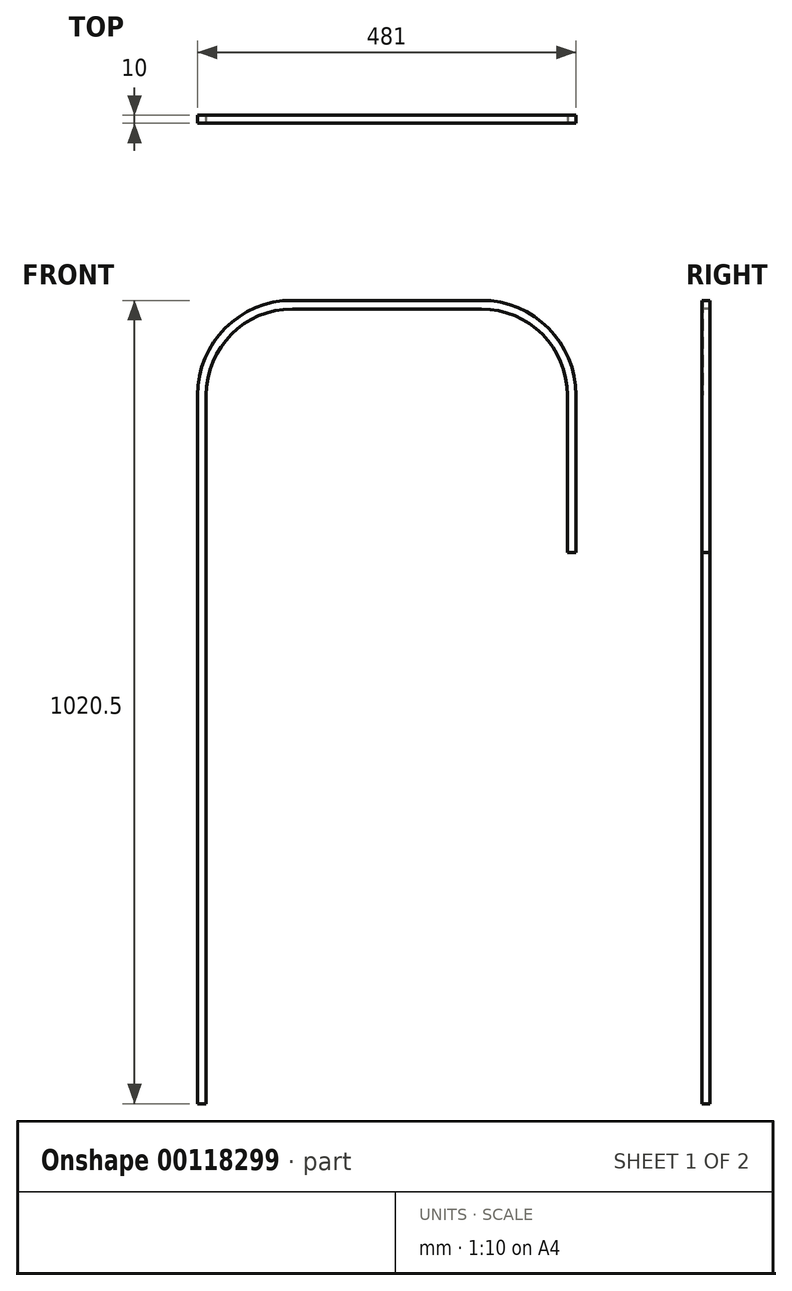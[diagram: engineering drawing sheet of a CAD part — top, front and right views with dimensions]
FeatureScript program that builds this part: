
annotation { "Feature Type Name" : "Feature", "Feature Type Description" : "" }
export const myFeature = defineFeature(function(context is Context, id is Id, definition is map)
    precondition{}
    {
        {
            var Q0;
            Q0=qCreatedBy(makeId("Front.planeOp"),FACE);
            var sketch = newSketch(context, id + "F0", { "sketchPlane" : qUnion([Q0])});
            skPoint(sketch, "E0.middle", {"position": v(15.73, 0) * mm});
            skLineSegment(sketch, "E1", {"start": v(-304.27, 450) * mm, "end": v(-302.77, 450) * mm});
            skLineSegment(sketch, "E2", {"start": v(197.23, 450) * mm, "end": v(198.73, 450) * mm});
            skLineSegment(sketch, "E3.0.left", {"start": v(-172.77, 570.5) * mm, "end": v(67.23, 570.5) * mm});
            skLineSegment(sketch, "E3.0.right", {"start": v(-172.77, 559.5) * mm, "end": v(67.23, 559.5) * mm});
            skArc(sketch, "E3.1.left", {"start": v(-172.77, 559.5) * mm, "mid": v(-250.2, 527.43) * mm, "end": v(-282.27, 450) * mm});
            skArc(sketch, "E3.1.right", {"start": v(-172.77, 570.5) * mm, "mid": v(-257.97, 535.2) * mm, "end": v(-293.27, 450) * mm});
            skArc(sketch, "E3.2.left", {"start": v(176.73, 450) * mm, "mid": v(144.66, 527.43) * mm, "end": v(67.23, 559.5) * mm});
            skArc(sketch, "E3.2.right", {"start": v(187.73, 450) * mm, "mid": v(152.44, 535.2) * mm, "end": v(67.23, 570.5) * mm});
            skLineSegment(sketch, "E3.3.left", {"start": v(176.73, -450) * mm, "end": v(176.73, 450) * mm});
            skLineSegment(sketch, "E3.3.right", {"start": v(187.73, -450) * mm, "end": v(187.73, 450) * mm});
            skLineSegment(sketch, "E3.4.left", {"start": v(-293.27, -450) * mm, "end": v(-293.27, 450) * mm});
            skLineSegment(sketch, "E3.4.right", {"start": v(-282.27, -450) * mm, "end": v(-282.27, 450) * mm});
            skLineSegment(sketch, "E4.0.left", {"start": v(-292.77, -450) * mm, "end": v(-292.77, 450) * mm});
            skLineSegment(sketch, "E4.0.right", {"start": v(-282.77, -450) * mm, "end": v(-282.77, 450) * mm});
            skArc(sketch, "E4.1.left", {"start": v(-172.77, 560) * mm, "mid": v(-250.55, 527.78) * mm, "end": v(-282.77, 450) * mm});
            skArc(sketch, "E4.1.right", {"start": v(-172.77, 570) * mm, "mid": v(-257.62, 534.85) * mm, "end": v(-292.77, 450) * mm});
            skLineSegment(sketch, "E4.2.left", {"start": v(-172.77, 570) * mm, "end": v(67.23, 570) * mm});
            skLineSegment(sketch, "E4.2.right", {"start": v(-172.77, 560) * mm, "end": v(67.23, 560) * mm});
            skArc(sketch, "E4.3.left", {"start": v(177.23, 450) * mm, "mid": v(145.02, 527.78) * mm, "end": v(67.23, 560) * mm});
            skArc(sketch, "E4.3.right", {"start": v(187.23, 450) * mm, "mid": v(152.09, 534.85) * mm, "end": v(67.23, 570) * mm});
            skLineSegment(sketch, "E4.4.left", {"start": v(177.23, -450) * mm, "end": v(177.23, 450) * mm});
            skLineSegment(sketch, "E4.4.right", {"start": v(187.23, -450) * mm, "end": v(187.23, 450) * mm});
            skLineSegment(sketch, "E5", {"start": v(187.23, -450) * mm, "end": v(177.23, -450) * mm});
            skLineSegment(sketch, "E6", {"start": v(-282.27, -450) * mm, "end": v(-293.27, -450) * mm});
            skLineSegment(sketch, "E7", {"start": v(-282.27, -450) * mm, "end": v(-282.77, -450) * mm});
            skLineSegment(sketch, "E8", {"start": v(-292.77, -450) * mm, "end": v(-293.27, -450) * mm});
            skLineSegment(sketch, "E9", {"start": v(187.73, -450) * mm, "end": v(176.73, -450) * mm});
            skLineSegment(sketch, "E10", {"start": v(187.23, -450) * mm, "end": v(187.73, -450) * mm});
            skLineSegment(sketch, "E11", {"start": v(-282.77, -450) * mm, "end": v(-292.77, -450) * mm});
            skLineSegment(sketch, "E12", {"start": v(177.23, -450) * mm, "end": v(176.73, -450) * mm});
            skSolve(sketch);
        }
        {
            var Q0;
            Q0=makeQuery(id+"F0.imprint","IMPRINT",FACE,{"disambiguationData":[TD([[makeQuery(id+"F0.imprint","IMPRINT",EDGE,{"derivedFrom":sQuery(id+"F0.wireOp",EDGE,"E3.0.left")}),-1.0]])]});
            var Q1;
            Q1=makeQuery(id+"F0.imprint","IMPRINT",FACE,{"disambiguationData":[TD([[makeQuery(id+"F0.imprint","IMPRINT",EDGE,{"derivedFrom":sQuery(id+"F0.wireOp",EDGE,"E3.0.right")}),1.0]])]});
            extrude(context, id + "F1", {"entities" : qUnion([Q0, Q1]), "oppositeDirection" : true, "depth" : 10 * mm});
        }
        {
            var Q0;
            Q0=makeQuery(id+"F0.imprint","IMPRINT",FACE,{"disambiguationData":[TD([[makeQuery(id+"F0.imprint","IMPRINT",EDGE,{"derivedFrom":sQuery(id+"F0.wireOp",EDGE,"E4.0.left")}),-1.0]])]});
            extrude(context, id + "F2", {"entities" : qUnion([Q0]), "operationType" : NewBodyOperationType.ADD, "oppositeDirection" : true, "depth" : 1 * mm});
        }
        {
            var Q0;
            Q0=makeQuery(id+"F2.boolean.opBoolean","MERGE",FACE,{"derivedFrom":[makeQuery(id+"F1.opExtrude","SWEPT_FACE",FACE,{"disambiguationData":[OSD([sQuery(id+"F0.wireOp",EDGE,"E10")])]}),makeQuery(id+"F1.opExtrude","SWEPT_FACE",FACE,{"disambiguationData":[OSD([sQuery(id+"F0.wireOp",EDGE,"E12")])]}),makeQuery(id+"F2.opExtrude","SWEPT_FACE",FACE,{"disambiguationData":[OSD([sQuery(id+"F0.wireOp",EDGE,"E5")])]})]});
            extrude(context, id + "F3", {"entities" : qUnion([Q0]), "operationType" : NewBodyOperationType.REMOVE, "oppositeDirection" : true, "depth" : 700 * mm});
        }
    });
